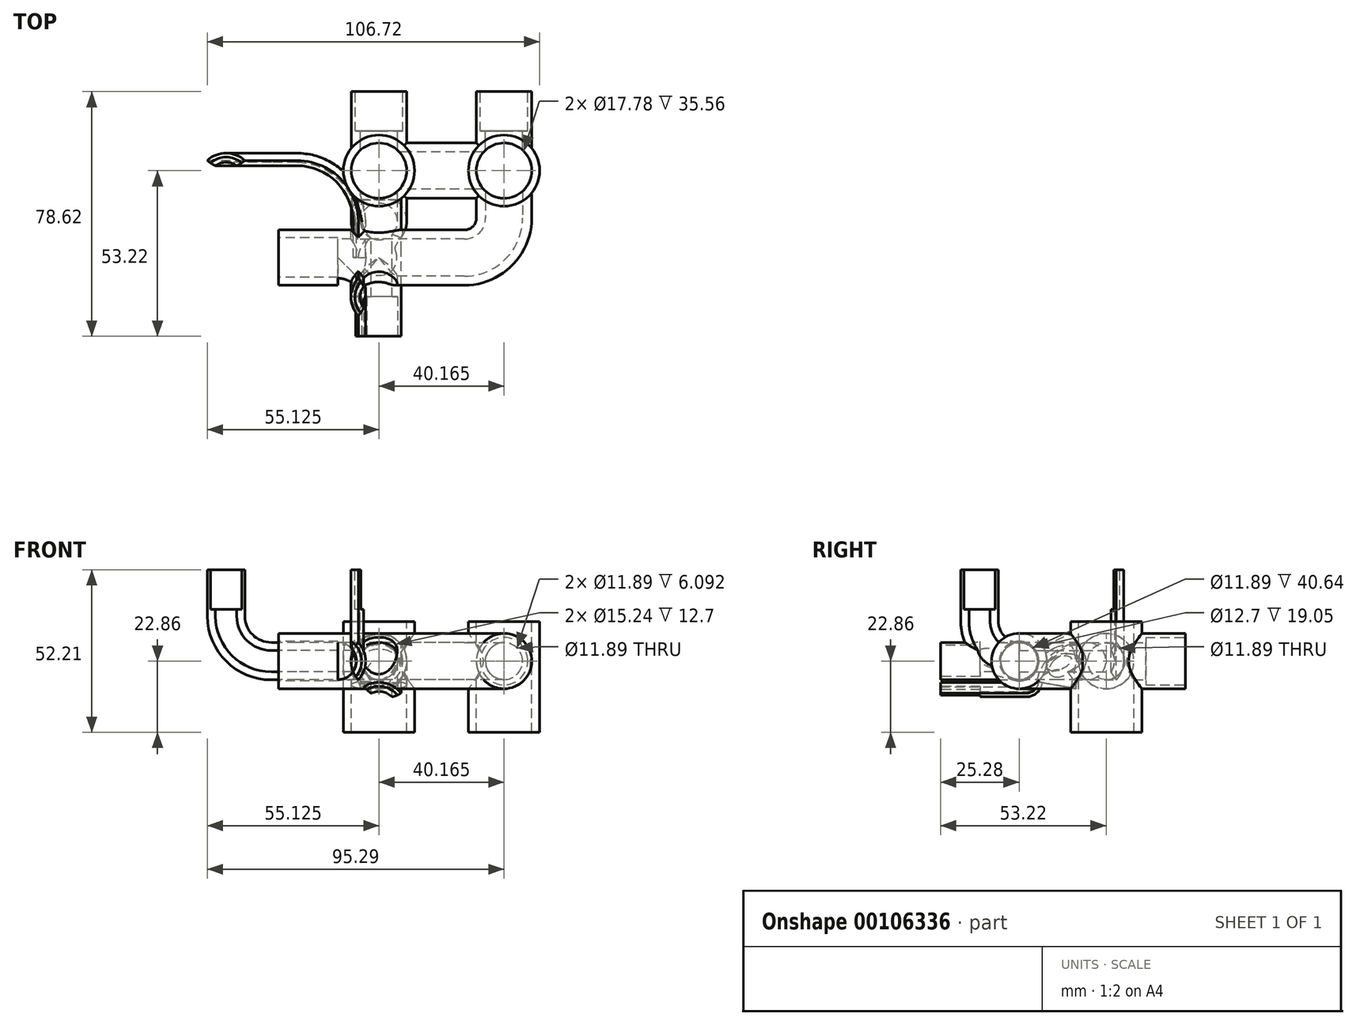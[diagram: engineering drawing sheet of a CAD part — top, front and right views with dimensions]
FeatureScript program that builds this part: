
annotation { "Feature Type Name" : "Feature", "Feature Type Description" : "" }
export const myFeature = defineFeature(function(context is Context, id is Id, definition is map)
    precondition{}
    {
        {
            var Q0;
            Q0=qCreatedBy(makeId("Front.planeOp"),FACE);
            var sketch = newSketch(context, id + "F0", { "sketchPlane" : qUnion([Q0])});
            skCircle(sketch, "E0", {"center": v(0, 0) * mm, "radius": 5.94 * mm});
            skCircle(sketch, "E1", {"center": v(0, 0) * mm, "radius": 8.9 * mm});
            skLineSegment(sketch, "E2", {"start": v(0, 0) * mm, "end": v(17.78, 0) * mm});
            skCircle(sketch, "E3", {"center": v(17.78, 0) * mm, "radius": 8.9 * mm});
            skCircle(sketch, "E4", {"center": v(17.78, 0) * mm, "radius": 5.94 * mm});
            skSolve(sketch);
        }
        {
            var Q0;
            Q0=qCreatedBy(makeId("Top.planeOp"),FACE);
            var sketch = newSketch(context, id + "F1", { "sketchPlane" : qUnion([Q0])});
            skLineSegment(sketch, "E5", {"start": v(0, 0) * mm, "end": v(0, -7.62) * mm});
            skLineSegment(sketch, "E6", {"start": v(17.78, 0) * mm, "end": v(17.78, -7.62) * mm});
            skArc(sketch, "E7", {"start": v(0, -7.62) * mm, "mid": v(-3.72, -16.6) * mm, "end": v(-12.7, -20.32) * mm});
            skLineSegment(sketch, "E8", {"start": v(-12.7, -20.32) * mm, "end": v(-53.34, -20.32) * mm});
            skLineSegment(sketch, "E9", {"start": v(-53.34, -20.32) * mm, "end": v(-53.34, -33.02) * mm});
            skArc(sketch, "E10", {"start": v(-53.34, -33.02) * mm, "mid": v(-50.36, -40.2) * mm, "end": v(-43.18, -43.18) * mm});
            skLineSegment(sketch, "E11", {"start": v(-43.18, -43.18) * mm, "end": v(-29.6, -43.18) * mm});
            skArc(sketch, "E12", {"start": v(0, -43.18) * mm, "mid": v(12.57, -37.97) * mm, "end": v(17.78, -25.4) * mm});
            skLineSegment(sketch, "E13", {"start": v(17.78, -25.4) * mm, "end": v(17.78, -7.62) * mm});
            skLineSegment(sketch, "E14", {"start": v(-43.18, -43.18) * mm, "end": v(-43.18, -20.32) * mm});
            skLineSegment(sketch, "E15", {"start": v(-43.18, -43.18) * mm, "end": v(-74.7, -43.18) * mm});
            skArc(sketch, "E16", {"start": v(-53.34, -20.32) * mm, "mid": v(-57.06, -11.34) * mm, "end": v(-66.04, -7.62) * mm});
            skLineSegment(sketch, "E17", {"start": v(17.78, -25.4) * mm, "end": v(17.78, -62.46) * mm});
            skArc(sketch, "E18", {"start": v(-21.28, -43.18) * mm, "mid": v(-12.34, -46.92) * mm, "end": v(-8.65, -55.88) * mm});
            skLineSegment(sketch, "E19", {"start": v(-8.65, -55.88) * mm, "end": v(-8.65, -62.46) * mm});
            skLineSegment(sketch, "E20", {"start": v(-8.65, -62.46) * mm, "end": v(17.78, -62.46) * mm});
            skLineSegment(sketch, "E21", {"start": v(-29.6, -43.18) * mm, "end": v(-21.28, -43.18) * mm});
            skLineSegment(sketch, "E22", {"start": v(-53.34, -20.32) * mm, "end": v(-53.34, -8.9) * mm});
            skArc(sketch, "E23", {"start": v(-53.34, -8.9) * mm, "mid": v(-57.21, 0.46) * mm, "end": v(-66.57, 4.34) * mm});
            skArc(sketch, "E24", {"start": v(-66.57, 4.34) * mm, "mid": v(-77.3, 9.13) * mm, "end": v(-80.9, 20.32) * mm});
            skLineSegment(sketch, "E25", {"start": v(-80.9, 20.32) * mm, "end": v(-80.9, 25.31) * mm});
            skLineSegment(sketch, "E26", {"start": v(-66.57, 4.34) * mm, "end": v(-72.83, 4.34) * mm});
            skSolve(sketch);
        }
        {
            var Q0;
            Q0=qCreatedBy(makeId("Front.planeOp"),FACE);
            cPlane(context, id + "F2", {"entities" : qUnion([Q0]), "cplaneType" : CPlaneType.OFFSET, "offset" : 20.32 * mm, "width" : 152.4 * mm, "height" : 152.4 * mm});
        }
        {
            var Q0;
            Q0=qCreatedBy(id+"F2.planeOp",FACE);
            var sketch = newSketch(context, id + "F3", { "sketchPlane" : qUnion([Q0])});
            skCircle(sketch, "E27", {"center": v(-53.34, 0) * mm, "radius": 8.9 * mm});
            skCircle(sketch, "E28", {"center": v(-53.34, 0) * mm, "radius": 5.94 * mm});
            skLineSegment(sketch, "E29", {"start": v(-47.4, 0) * mm, "end": v(-46.2, 0) * mm});
            skLineSegment(sketch, "E30", {"start": v(-46.2, 0) * mm, "end": v(-40.26, 0) * mm});
            skCircle(sketch, "E31", {"center": v(-40.26, 0) * mm, "radius": 5.94 * mm});
            skCircle(sketch, "E32", {"center": v(-40.26, 0) * mm, "radius": 8.9 * mm});
            skSolve(sketch);
        }
        {
            var Q0;
            Q0=qCreatedBy(makeId("Right.planeOp"),FACE);
            cPlane(context, id + "F4", {"entities" : qUnion([Q0]), "cplaneType" : CPlaneType.OFFSET, "offset" : 40.13 * mm, "oppositeDirection" : true, "width" : 152.4 * mm, "height" : 152.4 * mm});
        }
        {
            var Q0;
            Q0=qCreatedBy(id+"F4.planeOp",FACE);
            var sketch = newSketch(context, id + "F5", { "sketchPlane" : qUnion([Q0])});
            skLineSegment(sketch, "E33", {"start": v(-20.32, 0) * mm, "end": v(-20.35, 0) * mm});
            skArc(sketch, "E34", {"start": v(-20.35, 0) * mm, "mid": v(-29.33, 3.72) * mm, "end": v(-33.05, 12.7) * mm});
            skLineSegment(sketch, "E35", {"start": v(-33.05, 12.7) * mm, "end": v(-33.05, 16.67) * mm});
            skLineSegment(sketch, "E36", {"start": v(-20.32, 0) * mm, "end": v(-20.32, 16.9) * mm});
            skArc(sketch, "E37", {"start": v(-33.05, 16.67) * mm, "mid": v(-36.77, 25.65) * mm, "end": v(-45.75, 29.37) * mm});
            skLineSegment(sketch, "E38", {"start": v(-45.75, 29.37) * mm, "end": v(-51.61, 29.37) * mm});
            skLineSegment(sketch, "E39", {"start": v(-20.32, 0) * mm, "end": v(-35.47, 0) * mm});
            skLineSegment(sketch, "E40", {"start": v(-51.61, 29.37) * mm, "end": v(-51.61, 0) * mm});
            skSolve(sketch);
        }
        {
            var Q0;
            Q0=sQuery(id+"F1.wireOp",EDGE,"E9");
            cPlane(context, id + "F6", {"entities" : qUnion([Q0]), "cplaneType" : CPlaneType.LINE_ANGLE, "offset" : 25.4 * mm, "angle" : 315 * degree, "width" : 152.4 * mm, "height" : 152.4 * mm});
        }
        {
            var Q0;
            Q0=qCreatedBy(id+"F6.planeOp",FACE);
            var sketch = newSketch(context, id + "F7", { "sketchPlane" : qUnion([Q0])});
            skLineSegment(sketch, "E41", {"start": v(20.32, 37.72) * mm, "end": v(13.72, 37.72) * mm});
            skArc(sketch, "E42", {"start": v(13.72, 37.72) * mm, "mid": v(-7.04, 58.48) * mm, "end": v(13.72, 79.24) * mm});
            skLineSegment(sketch, "E43", {"start": v(13.72, 79.24) * mm, "end": v(51.6, 79.24) * mm});
            skSolve(sketch);
        }
        {
            var Q0;
            Q0=sQuery(id+"F7.wireOp",EDGE,"E43");
            cPlane(context, id + "F8", {"entities" : qUnion([Q0]), "cplaneType" : CPlaneType.LINE_ANGLE, "offset" : 25.4 * mm, "angle" : 90 * degree, "width" : 152.4 * mm, "height" : 152.4 * mm});
        }
        {
            var Q0;
            Q0=sQuery(id+"F7.wireOp",EDGE,"E43");
            cPlane(context, id + "F9", {"entities" : qUnion([Q0]), "cplaneType" : CPlaneType.LINE_ANGLE, "offset" : 25.4 * mm, "angle" : 0 * degree, "width" : 152.4 * mm, "height" : 152.4 * mm});
        }
        {
            var Q0;
            Q0=sQuery(id+"F1.wireOp",EDGE,"E9");
            cPlane(context, id + "F10", {"entities" : qUnion([Q0]), "cplaneType" : CPlaneType.LINE_ANGLE, "offset" : 25.4 * mm, "angle" : 310 * degree, "width" : 152.4 * mm, "height" : 152.4 * mm});
        }
        {
            var Q0;
            Q0=qCreatedBy(id+"F10.planeOp",FACE);
            var sketch = newSketch(context, id + "F11", { "sketchPlane" : qUnion([Q0])});
            skLineSegment(sketch, "E44", {"start": v(20.32, 34.29) * mm, "end": v(45.72, 34.29) * mm});
            skArc(sketch, "E45", {"start": v(45.72, 34.29) * mm, "mid": v(55.97, 24.04) * mm, "end": v(45.72, 13.79) * mm});
            skLineSegment(sketch, "E46", {"start": v(45.72, 13.79) * mm, "end": v(0, 13.79) * mm});
            skSolve(sketch);
        }
        {
            var Q0;
            Q0=sQuery(id+"F11.wireOp",EDGE,"E46");
            cPlane(context, id + "F12", {"entities" : qUnion([Q0]), "cplaneType" : CPlaneType.LINE_ANGLE, "offset" : 25.4 * mm, "angle" : 90 * degree, "width" : 152.4 * mm, "height" : 152.4 * mm});
        }
        {
            var Q0;
            Q0=qCreatedBy(id+"F12.planeOp",FACE);
            var sketch = newSketch(context, id + "F13", { "sketchPlane" : qUnion([Q0])});
            skLineSegment(sketch, "E47", {"start": v(-45.72, -15.7) * mm, "end": v(-18.13, -15.7) * mm});
            skArc(sketch, "E48", {"start": v(-18.13, -15.7) * mm, "mid": v(-11.95, -13.42) * mm, "end": v(-8.73, -7.66) * mm});
            skArc(sketch, "E49", {"start": v(-8.73, -7.66) * mm, "mid": v(-5.75, -2.25) * mm, "end": v(0, 0) * mm});
            skLineSegment(sketch, "E50", {"start": v(0, 0) * mm, "end": v(0, 3.02) * mm});
            skLineSegment(sketch, "E51", {"start": v(-18.13, -15.7) * mm, "end": v(0, -15.7) * mm});
            skLineSegment(sketch, "E52", {"start": v(0, 0) * mm, "end": v(0, -15.7) * mm});
            skSolve(sketch);
        }
        {
            var Q0;
            Q0=sQuery(id+"F13.wireOp",EDGE,"E50");
            cPlane(context, id + "F14", {"entities" : qUnion([Q0]), "cplaneType" : CPlaneType.LINE_ANGLE, "offset" : 25.4 * mm, "angle" : 90 * degree, "width" : 152.4 * mm, "height" : 152.4 * mm});
        }
        {
            var Q0;
            Q0=qCreatedBy(id+"F14.planeOp",FACE);
            var sketch = newSketch(context, id + "F15", { "sketchPlane" : qUnion([Q0])});
            skCircle(sketch, "E53", {"center": v(40.17, 0) * mm, "radius": 8.9 * mm});
            skCircle(sketch, "E54", {"center": v(40.17, 0) * mm, "radius": 5.94 * mm});
            skSolve(sketch);
        }
        {
            var Q0;
            {var subQ0=sQuery(id+"F3.wireOp",EDGE,"E32");var subQ1=sQuery(id+"F3.wireOp",EDGE,"E27");var subQ2=makeQuery(id+"F3.imprint","INTERSECT",VERTEX,{"disambiguationData":[OD(0.0)],"derivedFrom":[subQ1,subQ0]});Q0=makeQuery(id+"F3.imprint","IMPRINT",FACE,{"disambiguationData":[TD([[makeQuery(id+"F3.imprint","IMPRINT",EDGE,{"disambiguationData":[TD([[subQ2,-1.0]])],"derivedFrom":subQ1}),1.0]])]});}
            var Q1;
            {var subQ1=sQuery(id+"F3.wireOp",EDGE,"E29");Q1=makeQuery(id+"F3.imprint","IMPRINT",FACE,{"disambiguationData":[TD([[makeQuery(id+"F3.imprint","IMPRINT",EDGE,{"derivedFrom":subQ1}),1.0]])]});}
            var Q2;
            {var subQ0=sQuery(id+"F3.wireOp",EDGE,"E30");var subQ1=sQuery(id+"F3.wireOp",EDGE,"E27");var subQ2=makeQuery(id+"F3.imprint","INTERSECT",VERTEX,{"derivedFrom":[subQ1,subQ0]});Q2=makeQuery(id+"F3.imprint","IMPRINT",FACE,{"disambiguationData":[TD([[makeQuery(id+"F3.imprint","IMPRINT",EDGE,{"disambiguationData":[TD([[subQ2,-1.0]])],"derivedFrom":subQ1}),1.0]])]});}
            var Q3;
            {var subQ0=sQuery(id+"F3.wireOp",EDGE,"E30");var subQ1=sQuery(id+"F3.wireOp",EDGE,"E27");var subQ2=makeQuery(id+"F3.imprint","INTERSECT",VERTEX,{"derivedFrom":[subQ1,subQ0]});Q3=makeQuery(id+"F3.imprint","IMPRINT",FACE,{"disambiguationData":[TD([[makeQuery(id+"F3.imprint","IMPRINT",EDGE,{"disambiguationData":[TD([[subQ2,1.0]])],"derivedFrom":subQ1}),1.0]])]});}
            var Q4;
            {var subQ1=sQuery(id+"F3.wireOp",EDGE,"E29");Q4=makeQuery(id+"F3.imprint","IMPRINT",FACE,{"disambiguationData":[TD([[makeQuery(id+"F3.imprint","IMPRINT",EDGE,{"derivedFrom":subQ1}),-1.0]])]});}
            var Q5;
            Q5=sQuery(id+"F11.wireOp",EDGE,"E44");
            var Q6;
            Q6=sQuery(id+"F11.wireOp",EDGE,"E45");
            var Q7;
            Q7=sQuery(id+"F13.wireOp",EDGE,"E47");
            var Q8;
            Q8=sQuery(id+"F13.wireOp",EDGE,"E48");
            var Q9;
            Q9=sQuery(id+"F13.wireOp",EDGE,"E49");
            sweep(context, id + "F16", {"profiles" : qUnion([Q0, Q1, Q2, Q3, Q4]), "path" : qUnion([Q5, Q6, Q7, Q8, Q9])});
        }
        {
            var Q0;
            Q0=makeQuery(id+"F15.imprint","IMPRINT",FACE,{"disambiguationData":[TD([[makeQuery(id+"F15.imprint","IMPRINT",EDGE,{"derivedFrom":sQuery(id+"F15.wireOp",EDGE,"E53")}),1.0]])]});
            var Q1;
            Q1=sQuery(id+"F13.wireOp",EDGE,"E49");
            sweep(context, id + "F17", {"operationType" : NewBodyOperationType.ADD, "profiles" : qUnion([Q0]), "path" : qUnion([Q1])});
        }
        {
            var Q0;
            {var subQ0=sQuery(id+"F3.wireOp",EDGE,"E32");var subQ1=sQuery(id+"F3.wireOp",EDGE,"E27");var subQ2=makeQuery(id+"F3.imprint","INTERSECT",VERTEX,{"disambiguationData":[OD(0.0)],"derivedFrom":[subQ1,subQ0]});Q0=makeQuery(id+"F3.imprint","IMPRINT",FACE,{"disambiguationData":[TD([[makeQuery(id+"F3.imprint","IMPRINT",EDGE,{"disambiguationData":[TD([[subQ2,1.0]])],"derivedFrom":subQ1}),-1.0]])]});}
            var Q1;
            {var subQ1=sQuery(id+"F3.wireOp",EDGE,"E29");Q1=makeQuery(id+"F3.imprint","IMPRINT",FACE,{"disambiguationData":[TD([[makeQuery(id+"F3.imprint","IMPRINT",EDGE,{"derivedFrom":subQ1}),1.0]])]});}
            var Q2;
            {var subQ0=sQuery(id+"F3.wireOp",EDGE,"E28");var subQ1=makeQuery(id+"F3.imprint","INTERSECT",VERTEX,{"derivedFrom":[subQ0,sQuery(id+"F3.wireOp",EDGE,"E29")]});Q2=makeQuery(id+"F3.imprint","IMPRINT",FACE,{"disambiguationData":[TD([[makeQuery(id+"F3.imprint","IMPRINT",EDGE,{"disambiguationData":[TD([[subQ1,-1.0]])],"derivedFrom":subQ0}),1.0]])]});}
            var Q3;
            {var subQ1=sQuery(id+"F3.wireOp",EDGE,"E29");Q3=makeQuery(id+"F3.imprint","IMPRINT",FACE,{"disambiguationData":[TD([[makeQuery(id+"F3.imprint","IMPRINT",EDGE,{"derivedFrom":subQ1}),-1.0]])]});}
            var Q4;
            Q4=sQuery(id+"F5.wireOp",EDGE,"E34");
            var Q5;
            Q5=sQuery(id+"F5.wireOp",EDGE,"E35");
            sweep(context, id + "F18", {"operationType" : NewBodyOperationType.ADD, "profiles" : qUnion([Q0, Q1, Q2, Q3]), "path" : qUnion([Q4, Q5])});
        }
        {
            var Q0;
            {var subQ0=sQuery(id+"F3.wireOp",EDGE,"E28");var subQ1=makeQuery(id+"F3.imprint","INTERSECT",VERTEX,{"derivedFrom":[subQ0,sQuery(id+"F3.wireOp",EDGE,"E29")]});Q0=makeQuery(id+"F3.imprint","IMPRINT",FACE,{"disambiguationData":[TD([[makeQuery(id+"F3.imprint","IMPRINT",EDGE,{"disambiguationData":[TD([[subQ1,-1.0]])],"derivedFrom":subQ0}),1.0]])]});}
            var Q1;
            {var subQ1=sQuery(id+"F3.wireOp",EDGE,"E29");Q1=makeQuery(id+"F3.imprint","IMPRINT",FACE,{"disambiguationData":[TD([[makeQuery(id+"F3.imprint","IMPRINT",EDGE,{"derivedFrom":subQ1}),1.0]])]});}
            var Q2;
            {var subQ0=sQuery(id+"F3.wireOp",EDGE,"E32");var subQ1=sQuery(id+"F3.wireOp",EDGE,"E27");var subQ2=makeQuery(id+"F3.imprint","INTERSECT",VERTEX,{"disambiguationData":[OD(0.0)],"derivedFrom":[subQ1,subQ0]});Q2=makeQuery(id+"F3.imprint","IMPRINT",FACE,{"disambiguationData":[TD([[makeQuery(id+"F3.imprint","IMPRINT",EDGE,{"disambiguationData":[TD([[subQ2,1.0]])],"derivedFrom":subQ1}),-1.0]])]});}
            var Q3;
            {var subQ1=sQuery(id+"F3.wireOp",EDGE,"E29");Q3=makeQuery(id+"F3.imprint","IMPRINT",FACE,{"disambiguationData":[TD([[makeQuery(id+"F3.imprint","IMPRINT",EDGE,{"derivedFrom":subQ1}),-1.0]])]});}
            var Q4;
            Q4=sQuery(id+"F5.wireOp",EDGE,"E34");
            var Q5;
            Q5=sQuery(id+"F5.wireOp",EDGE,"E35");
            sweep(context, id + "F19", {"operationType" : NewBodyOperationType.ADD, "profiles" : qUnion([Q0, Q1, Q2, Q3]), "path" : qUnion([Q4, Q5])});
        }
        {
            var Q0;
            Q0=sQuery(id+"F1.wireOp",EDGE,"E9");
            cPlane(context, id + "F20", {"entities" : qUnion([Q0]), "cplaneType" : CPlaneType.LINE_ANGLE, "offset" : 25.4 * mm, "angle" : 90 * degree, "width" : 152.4 * mm, "height" : 152.4 * mm});
        }
        {
            var Q0;
            Q0=qCreatedBy(id+"F20.planeOp",FACE);
            var sketch = newSketch(context, id + "F21", { "sketchPlane" : qUnion([Q0])});
            skCircle(sketch, "E55", {"center": v(-20.32, 0) * mm, "radius": 6.35 * mm});
            skCircle(sketch, "E56", {"center": v(-20.32, 0) * mm, "radius": 8.9 * mm});
            skSolve(sketch);
        }
        {
            var Q0;
            Q0=qCreatedBy(makeId("Top.planeOp"),FACE);
            var sketch = newSketch(context, id + "F22", { "sketchPlane" : qUnion([Q0])});
            skLineSegment(sketch, "E57", {"start": v(-53.34, -20.32) * mm, "end": v(-72.4, -20.32) * mm});
            skSolve(sketch);
        }
        {
            var Q0;
            Q0=makeQuery(id+"F0.imprint","IMPRINT",FACE,{"disambiguationData":[TD([[makeQuery(id+"F0.imprint","IMPRINT",EDGE,{"derivedFrom":sQuery(id+"F0.wireOp",EDGE,"E0")}),1.0]])]});
            var Q1;
            Q1=sQuery(id+"F1.wireOp",EDGE,"E5");
            var Q2;
            Q2=sQuery(id+"F1.wireOp",EDGE,"E7");
            var Q3;
            Q3=sQuery(id+"F1.wireOp",EDGE,"E8");
            sweep(context, id + "F23", {"operationType" : NewBodyOperationType.REMOVE, "profiles" : qUnion([Q0]), "path" : qUnion([Q1, Q2, Q3])});
        }
        {
            var Q0;
            Q0=makeQuery(id+"F0.imprint","IMPRINT",FACE,{"disambiguationData":[TD([[makeQuery(id+"F0.imprint","IMPRINT",EDGE,{"derivedFrom":sQuery(id+"F0.wireOp",EDGE,"E0")}),-1.0]])]});
            var Q1;
            Q1=sQuery(id+"F1.wireOp",EDGE,"E5");
            var Q2;
            Q2=sQuery(id+"F1.wireOp",EDGE,"E7");
            var Q3;
            Q3=sQuery(id+"F1.wireOp",EDGE,"E8");
            sweep(context, id + "F24", {"operationType" : NewBodyOperationType.ADD, "profiles" : qUnion([Q0]), "path" : qUnion([Q1, Q2, Q3])});
        }
        {
            var Q0;
            Q0=makeQuery(id+"F15.imprint","IMPRINT",FACE,{"disambiguationData":[TD([[makeQuery(id+"F15.imprint","IMPRINT",EDGE,{"derivedFrom":sQuery(id+"F15.wireOp",EDGE,"E54")}),1.0]])]});
            var Q1;
            Q1=sQuery(id+"F11.wireOp",EDGE,"E44");
            var Q2;
            Q2=sQuery(id+"F11.wireOp",EDGE,"E45");
            var Q3;
            Q3=sQuery(id+"F13.wireOp",EDGE,"E49");
            var Q4;
            Q4=sQuery(id+"F13.wireOp",EDGE,"E48");
            var Q5;
            Q5=sQuery(id+"F13.wireOp",EDGE,"E47");
            sweep(context, id + "F25", {"operationType" : NewBodyOperationType.REMOVE, "profiles" : qUnion([Q0]), "path" : qUnion([Q1, Q2, Q3, Q4, Q5])});
        }
        {
            var Q0;
            {var subQ0=sQuery(id+"F3.wireOp",EDGE,"E27");var subQ1=makeQuery(id+"F3.imprint","INTERSECT",VERTEX,{"derivedFrom":[subQ0,sQuery(id+"F3.wireOp",EDGE,"E30")]});Q0=makeQuery(id+"F3.imprint","IMPRINT",FACE,{"disambiguationData":[TD([[makeQuery(id+"F3.imprint","IMPRINT",EDGE,{"disambiguationData":[TD([[subQ1,-1.0]])],"derivedFrom":subQ0}),-1.0]])]});}
            var Q1;
            {var subQ0=sQuery(id+"F3.wireOp",EDGE,"E30");var subQ1=sQuery(id+"F3.wireOp",EDGE,"E27");var subQ2=makeQuery(id+"F3.imprint","INTERSECT",VERTEX,{"derivedFrom":[subQ1,subQ0]});Q1=makeQuery(id+"F3.imprint","IMPRINT",FACE,{"disambiguationData":[TD([[makeQuery(id+"F3.imprint","IMPRINT",EDGE,{"disambiguationData":[TD([[subQ2,-1.0]])],"derivedFrom":subQ1}),1.0]])]});}
            var Q2;
            {var subQ0=sQuery(id+"F3.wireOp",EDGE,"E30");var subQ1=sQuery(id+"F3.wireOp",EDGE,"E27");var subQ2=makeQuery(id+"F3.imprint","INTERSECT",VERTEX,{"derivedFrom":[subQ1,subQ0]});Q2=makeQuery(id+"F3.imprint","IMPRINT",FACE,{"disambiguationData":[TD([[makeQuery(id+"F3.imprint","IMPRINT",EDGE,{"disambiguationData":[TD([[subQ2,1.0]])],"derivedFrom":subQ1}),1.0]])]});}
            var Q3;
            Q3=sQuery(id+"F5.wireOp",EDGE,"E34");
            var Q4;
            Q4=sQuery(id+"F5.wireOp",EDGE,"E35");
            var Q5;
            Q5=sQuery(id+"F5.wireOp",EDGE,"E37");
            sweep(context, id + "F26", {"operationType" : NewBodyOperationType.REMOVE, "profiles" : qUnion([Q0, Q1, Q2]), "path" : qUnion([Q3, Q4, Q5])});
        }
        {
            var Q0;
            Q0=makeQuery(id+"F21.imprint","IMPRINT",FACE,{"disambiguationData":[TD([[makeQuery(id+"F21.imprint","IMPRINT",EDGE,{"derivedFrom":sQuery(id+"F21.wireOp",EDGE,"E55")}),1.0]])]});
            var Q1;
            Q1=sQuery(id+"F22.wireOp",EDGE,"E57");
            sweep(context, id + "F27", {"operationType" : NewBodyOperationType.REMOVE, "profiles" : qUnion([Q0]), "path" : qUnion([Q1])});
        }
        {
            var Q0;
            {var subQ0=sQuery(id+"F3.wireOp",EDGE,"E32");var subQ1=sQuery(id+"F3.wireOp",EDGE,"E28");var subQ2=makeQuery(id+"F3.imprint","INTERSECT",VERTEX,{"disambiguationData":[OD(0.0)],"derivedFrom":[subQ1,subQ0]});Q0=makeQuery(id+"F3.imprint","IMPRINT",FACE,{"disambiguationData":[TD([[makeQuery(id+"F3.imprint","IMPRINT",EDGE,{"disambiguationData":[TD([[subQ2,-1.0]])],"derivedFrom":subQ1}),1.0]])]});}
            var Q1;
            {var subQ0=sQuery(id+"F3.wireOp",EDGE,"E28");var subQ1=makeQuery(id+"F3.imprint","INTERSECT",VERTEX,{"derivedFrom":[subQ0,sQuery(id+"F3.wireOp",EDGE,"E29")]});Q1=makeQuery(id+"F3.imprint","IMPRINT",FACE,{"disambiguationData":[TD([[makeQuery(id+"F3.imprint","IMPRINT",EDGE,{"disambiguationData":[TD([[subQ1,-1.0]])],"derivedFrom":subQ0}),1.0]])]});}
            var Q2;
            Q2=sQuery(id+"F7.wireOp",EDGE,"E41");
            var Q3;
            Q3=sQuery(id+"F7.wireOp",EDGE,"E42");
            sweep(context, id + "F28", {"operationType" : NewBodyOperationType.REMOVE, "profiles" : qUnion([Q0, Q1]), "path" : qUnion([Q2, Q3])});
        }
        {
            var Q0;
            Q0=makeQuery(id+"F21.imprint","IMPRINT",FACE,{"disambiguationData":[TD([[makeQuery(id+"F21.imprint","IMPRINT",EDGE,{"derivedFrom":sQuery(id+"F21.wireOp",EDGE,"E55")}),-1.0]])]});
            var Q1;
            Q1=sQuery(id+"F22.wireOp",EDGE,"E57");
            sweep(context, id + "F29", {"operationType" : NewBodyOperationType.ADD, "profiles" : qUnion([Q0]), "path" : qUnion([Q1])});
        }
        {
            var Q0;
            {var subQ0=sQuery(id+"F3.wireOp",EDGE,"E32");var subQ1=sQuery(id+"F3.wireOp",EDGE,"E28");var subQ2=makeQuery(id+"F3.imprint","INTERSECT",VERTEX,{"disambiguationData":[OD(0.0)],"derivedFrom":[subQ1,subQ0]});Q0=makeQuery(id+"F3.imprint","IMPRINT",FACE,{"disambiguationData":[TD([[makeQuery(id+"F3.imprint","IMPRINT",EDGE,{"disambiguationData":[TD([[subQ2,-1.0]])],"derivedFrom":subQ1}),1.0]])]});}
            var Q1;
            {var subQ0=sQuery(id+"F3.wireOp",EDGE,"E28");var subQ1=makeQuery(id+"F3.imprint","INTERSECT",VERTEX,{"derivedFrom":[subQ0,sQuery(id+"F3.wireOp",EDGE,"E29")]});Q1=makeQuery(id+"F3.imprint","IMPRINT",FACE,{"disambiguationData":[TD([[makeQuery(id+"F3.imprint","IMPRINT",EDGE,{"disambiguationData":[TD([[subQ1,-1.0]])],"derivedFrom":subQ0}),1.0]])]});}
            var Q2;
            Q2=sQuery(id+"F7.wireOp",EDGE,"E42");
            var Q3;
            Q3=sQuery(id+"F7.wireOp",EDGE,"E41");
            sweep(context, id + "F30", {"operationType" : NewBodyOperationType.REMOVE, "profiles" : qUnion([Q0, Q1]), "path" : qUnion([Q2, Q3])});
        }
        {
            var Q0;
            {var subQ0=sQuery(id+"F3.wireOp",EDGE,"E32");var subQ1=sQuery(id+"F3.wireOp",EDGE,"E28");var subQ2=makeQuery(id+"F3.imprint","INTERSECT",VERTEX,{"disambiguationData":[OD(0.0)],"derivedFrom":[subQ1,subQ0]});Q0=makeQuery(id+"F3.imprint","IMPRINT",FACE,{"disambiguationData":[TD([[makeQuery(id+"F3.imprint","IMPRINT",EDGE,{"disambiguationData":[TD([[subQ2,-1.0]])],"derivedFrom":subQ1}),1.0]])]});}
            var Q1;
            {var subQ0=sQuery(id+"F3.wireOp",EDGE,"E28");var subQ1=makeQuery(id+"F3.imprint","INTERSECT",VERTEX,{"derivedFrom":[subQ0,sQuery(id+"F3.wireOp",EDGE,"E29")]});Q1=makeQuery(id+"F3.imprint","IMPRINT",FACE,{"disambiguationData":[TD([[makeQuery(id+"F3.imprint","IMPRINT",EDGE,{"disambiguationData":[TD([[subQ1,-1.0]])],"derivedFrom":subQ0}),1.0]])]});}
            var Q2;
            Q2=sQuery(id+"F11.wireOp",EDGE,"E45");
            var Q3;
            Q3=sQuery(id+"F11.wireOp",EDGE,"E44");
            sweep(context, id + "F31", {"operationType" : NewBodyOperationType.REMOVE, "profiles" : qUnion([Q0, Q1]), "path" : qUnion([Q2, Q3])});
        }
        {
            var Q0;
            Q0=qCreatedBy(makeId("Top.planeOp"),FACE);
            var sketch = newSketch(context, id + "F32", { "sketchPlane" : qUnion([Q0])});
            skLineSegment(sketch, "E58", {"start": v(0, 0) * mm, "end": v(0, 7.62) * mm});
            skLineSegment(sketch, "E59", {"start": v(-40.17, 0) * mm, "end": v(-40.17, 7.62) * mm});
            skCircle(sketch, "E60", {"center": v(-40.17, 7.62) * mm, "radius": 8.9 * mm});
            skCircle(sketch, "E61", {"center": v(0, 7.62) * mm, "radius": 8.9 * mm});
            skCircle(sketch, "E62", {"center": v(0, 7.62) * mm, "radius": 11.43 * mm});
            skCircle(sketch, "E63", {"center": v(-40.17, 7.62) * mm, "radius": 11.43 * mm});
            skSolve(sketch);
        }
        {
            var Q0;
            Q0=sQuery(id+"F32.wireOp",EDGE,"E59");
            cPlane(context, id + "F33", {"entities" : qUnion([Q0]), "cplaneType" : CPlaneType.LINE_ANGLE, "offset" : 25.4 * mm, "angle" : 90 * degree, "width" : 152.4 * mm, "height" : 152.4 * mm});
        }
        {
            var Q0;
            Q0=qCreatedBy(id+"F33.planeOp",FACE);
            var sketch = newSketch(context, id + "F34", { "sketchPlane" : qUnion([Q0])});
            skLineSegment(sketch, "E64", {"start": v(7.62, 0) * mm, "end": v(7.62, 4.48) * mm});
            skSolve(sketch);
        }
        {
            var Q0;
            Q0=sQuery(id+"F34.wireOp",EDGE,"E64");
            cPlane(context, id + "F35", {"entities" : qUnion([Q0]), "cplaneType" : CPlaneType.LINE_ANGLE, "offset" : 25.4 * mm, "angle" : 135 * degree, "width" : 152.4 * mm, "height" : 152.4 * mm});
        }
        {
            var Q0;
            Q0=makeQuery(id+"F32.imprint","IMPRINT",FACE,{"disambiguationData":[TD([[makeQuery(id+"F32.imprint","IMPRINT",EDGE,{"derivedFrom":sQuery(id+"F32.wireOp",EDGE,"E60")}),-1.0]])]});
            extrude(context, id + "F36", {"entities" : qUnion([Q0]), "operationType" : NewBodyOperationType.ADD, "oppositeDirection" : true, "depth" : 22.86 * mm});
        }
        {
            var Q0;
            Q0=makeQuery(id+"F32.imprint","IMPRINT",FACE,{"disambiguationData":[TD([[makeQuery(id+"F32.imprint","IMPRINT",EDGE,{"derivedFrom":sQuery(id+"F32.wireOp",EDGE,"E61")}),-1.0]])]});
            extrude(context, id + "F37", {"entities" : qUnion([Q0]), "operationType" : NewBodyOperationType.ADD, "oppositeDirection" : true, "depth" : 22.86 * mm});
        }
        {
            var Q0;
            Q0=qCreatedBy(makeId("Front.planeOp"),FACE);
            cPlane(context, id + "F38", {"entities" : qUnion([Q0]), "cplaneType" : CPlaneType.OFFSET, "offset" : 7.62 * mm, "oppositeDirection" : true, "width" : 152.4 * mm, "height" : 152.4 * mm});
        }
        {
            var Q0;
            Q0=makeQuery(id+"F32.imprint","IMPRINT",FACE,{"disambiguationData":[TD([[makeQuery(id+"F32.imprint","IMPRINT",EDGE,{"derivedFrom":sQuery(id+"F32.wireOp",EDGE,"E61")}),-1.0]])]});
            extrude(context, id + "F39", {"entities" : qUnion([Q0]), "operationType" : NewBodyOperationType.ADD, "depth" : 12.7 * mm});
        }
        {
            var Q0;
            Q0=makeQuery(id+"F32.imprint","IMPRINT",FACE,{"disambiguationData":[TD([[makeQuery(id+"F32.imprint","IMPRINT",EDGE,{"derivedFrom":sQuery(id+"F32.wireOp",EDGE,"E60")}),-1.0]])]});
            extrude(context, id + "F40", {"entities" : qUnion([Q0]), "operationType" : NewBodyOperationType.ADD, "depth" : 12.7 * mm});
        }
        {
            var Q0;
            Q0=qCreatedBy(makeId("Right.planeOp"),FACE);
            var sketch = newSketch(context, id + "F41", { "sketchPlane" : qUnion([Q0])});
            skCircle(sketch, "E65", {"center": v(7.62, 0) * mm, "radius": 5.94 * mm});
            skCircle(sketch, "E66", {"center": v(7.62, 0) * mm, "radius": 8.9 * mm});
            skSolve(sketch);
        }
        {
            var Q0;
            Q0=qCreatedBy(makeId("Top.planeOp"),FACE);
            var sketch = newSketch(context, id + "F42", { "sketchPlane" : qUnion([Q0])});
            skLineSegment(sketch, "E67", {"start": v(0, 7.62) * mm, "end": v(-40.17, 7.62) * mm});
            skSolve(sketch);
        }
        {
            var Q0;
            Q0=qCreatedBy(id+"F38.planeOp",FACE);
            var sketch = newSketch(context, id + "F43", { "sketchPlane" : qUnion([Q0])});
            skCircle(sketch, "E68", {"center": v(-40.17, 0) * mm, "radius": 5.94 * mm});
            skCircle(sketch, "E69", {"center": v(-40.17, 0) * mm, "radius": 8.9 * mm});
            skCircle(sketch, "E70", {"center": v(0, 0) * mm, "radius": 5.94 * mm});
            skCircle(sketch, "E71", {"center": v(0, 0) * mm, "radius": 8.9 * mm});
            skSolve(sketch);
        }
        {
            var Q0;
            Q0=qCreatedBy(makeId("Top.planeOp"),FACE);
            var sketch = newSketch(context, id + "F44", { "sketchPlane" : qUnion([Q0])});
            skLineSegment(sketch, "E72", {"start": v(0, 7.62) * mm, "end": v(0, 33.02) * mm});
            skLineSegment(sketch, "E73", {"start": v(-40.17, 7.62) * mm, "end": v(-40.17, 33.02) * mm});
            skSolve(sketch);
        }
        {
            var Q0;
            Q0=makeQuery(id+"F43.imprint","IMPRINT",FACE,{"disambiguationData":[TD([[makeQuery(id+"F43.imprint","IMPRINT",EDGE,{"derivedFrom":sQuery(id+"F43.wireOp",EDGE,"E70")}),-1.0]])]});
            var Q1;
            Q1=sQuery(id+"F44.wireOp",EDGE,"E72");
            sweep(context, id + "F45", {"operationType" : NewBodyOperationType.ADD, "profiles" : qUnion([Q0]), "path" : qUnion([Q1])});
        }
        {
            var Q0;
            Q0=makeQuery(id+"F43.imprint","IMPRINT",FACE,{"disambiguationData":[TD([[makeQuery(id+"F43.imprint","IMPRINT",EDGE,{"derivedFrom":sQuery(id+"F43.wireOp",EDGE,"E68")}),-1.0]])]});
            var Q1;
            Q1=sQuery(id+"F44.wireOp",EDGE,"E73");
            sweep(context, id + "F46", {"operationType" : NewBodyOperationType.ADD, "profiles" : qUnion([Q0]), "path" : qUnion([Q1])});
        }
        {
            var Q0;
            Q0=makeQuery(id+"F41.imprint","IMPRINT",FACE,{"disambiguationData":[TD([[makeQuery(id+"F41.imprint","IMPRINT",EDGE,{"derivedFrom":sQuery(id+"F41.wireOp",EDGE,"E65")}),-1.0]])]});
            var Q1;
            Q1=sQuery(id+"F42.wireOp",EDGE,"E67");
            sweep(context, id + "F47", {"operationType" : NewBodyOperationType.ADD, "profiles" : qUnion([Q0]), "path" : qUnion([Q1])});
        }
        {
            var Q0;
            Q0=makeQuery(id+"F32.imprint","IMPRINT",FACE,{"disambiguationData":[TD([[makeQuery(id+"F32.imprint","IMPRINT",EDGE,{"derivedFrom":sQuery(id+"F32.wireOp",EDGE,"E61")}),1.0]])]});
            extrude(context, id + "F48", {"entities" : qUnion([Q0]), "operationType" : NewBodyOperationType.REMOVE, "oppositeDirection" : true, "depth" : 25.4 * mm});
        }
        {
            var Q0;
            Q0=makeQuery(id+"F32.imprint","IMPRINT",FACE,{"disambiguationData":[TD([[makeQuery(id+"F32.imprint","IMPRINT",EDGE,{"derivedFrom":sQuery(id+"F32.wireOp",EDGE,"E61")}),1.0]])]});
            extrude(context, id + "F49", {"entities" : qUnion([Q0]), "operationType" : NewBodyOperationType.REMOVE, "depth" : 25.4 * mm});
        }
        {
            var Q0;
            Q0=makeQuery(id+"F32.imprint","IMPRINT",FACE,{"disambiguationData":[TD([[makeQuery(id+"F32.imprint","IMPRINT",EDGE,{"derivedFrom":sQuery(id+"F32.wireOp",EDGE,"E60")}),1.0]])]});
            var Q1;
            Q1=sQuery(id+"F32.wireOp",EDGE,"E60");
            extrude(context, id + "F50", {"entities" : qUnion([Q0]), "operationType" : NewBodyOperationType.REMOVE, "surfaceEntities" : qUnion([Q1]), "depth" : 25.4 * mm});
        }
        {
            var Q0;
            Q0=makeQuery(id+"F32.imprint","IMPRINT",FACE,{"disambiguationData":[TD([[makeQuery(id+"F32.imprint","IMPRINT",EDGE,{"derivedFrom":sQuery(id+"F32.wireOp",EDGE,"E60")}),1.0]])]});
            extrude(context, id + "F51", {"entities" : qUnion([Q0]), "operationType" : NewBodyOperationType.REMOVE, "oppositeDirection" : true, "depth" : 25.4 * mm});
        }
        {
            var Q0;
            Q0=makeQuery(id+"F43.imprint","IMPRINT",FACE,{"disambiguationData":[TD([[makeQuery(id+"F43.imprint","IMPRINT",EDGE,{"derivedFrom":sQuery(id+"F43.wireOp",EDGE,"E70")}),1.0]])]});
            extrude(context, id + "F52", {"entities" : qUnion([Q0]), "operationType" : NewBodyOperationType.REMOVE, "oppositeDirection" : true, "depth" : 25.4 * mm});
        }
        {
            var Q0;
            Q0=makeQuery(id+"F43.imprint","IMPRINT",FACE,{"disambiguationData":[TD([[makeQuery(id+"F43.imprint","IMPRINT",EDGE,{"derivedFrom":sQuery(id+"F43.wireOp",EDGE,"E68")}),1.0]])]});
            extrude(context, id + "F53", {"entities" : qUnion([Q0]), "operationType" : NewBodyOperationType.REMOVE, "oppositeDirection" : true, "depth" : 34.24 * mm});
        }
        {
            var Q0;
            Q0=makeQuery(id+"F41.imprint","IMPRINT",FACE,{"disambiguationData":[TD([[makeQuery(id+"F41.imprint","IMPRINT",EDGE,{"derivedFrom":sQuery(id+"F41.wireOp",EDGE,"E65")}),1.0]])]});
            extrude(context, id + "F54", {"entities" : qUnion([Q0]), "operationType" : NewBodyOperationType.REMOVE, "oppositeDirection" : true, "depth" : 35.6 * mm});
        }
        {
            var Q0;
            Q0=makeQuery(id+"F43.imprint","IMPRINT",FACE,{"disambiguationData":[TD([[makeQuery(id+"F43.imprint","IMPRINT",EDGE,{"derivedFrom":sQuery(id+"F43.wireOp",EDGE,"E70")}),1.0]])]});
            extrude(context, id + "F55", {"entities" : qUnion([Q0]), "operationType" : NewBodyOperationType.REMOVE, "depth" : 13.84 * mm});
        }
        {
            var Q0;
            Q0=makeQuery(id+"F15.imprint","IMPRINT",FACE,{"disambiguationData":[TD([[makeQuery(id+"F15.imprint","IMPRINT",EDGE,{"derivedFrom":sQuery(id+"F15.wireOp",EDGE,"E54")}),1.0]])]});
            var Q1;
            Q1=sQuery(id+"F15.wireOp",EDGE,"E54");
            var Q2;
            Q2=sQuery(id+"F13.wireOp",EDGE,"E49");
            sweep(context, id + "F56", {"operationType" : NewBodyOperationType.REMOVE, "profiles" : qUnion([Q0]), "surfaceProfiles" : qUnion([Q1]), "path" : qUnion([Q2])});
        }
        {
            var Q0;
            Q0=makeQuery(id+"F43.imprint","IMPRINT",FACE,{"disambiguationData":[TD([[makeQuery(id+"F43.imprint","IMPRINT",EDGE,{"derivedFrom":sQuery(id+"F43.wireOp",EDGE,"E68")}),1.0]])]});
            var Q1;
            Q1=sQuery(id+"F43.wireOp",EDGE,"E68");
            extrude(context, id + "F57", {"entities" : qUnion([Q0]), "operationType" : NewBodyOperationType.REMOVE, "surfaceEntities" : qUnion([Q1]), "depth" : 9.43 * mm});
        }
        {
            var Q0;
            Q0=qCreatedBy(makeId("Top.planeOp"),FACE);
            var sketch = newSketch(context, id + "F58", { "sketchPlane" : qUnion([Q0])});
            skLineSegment(sketch, "E74.bottom", {"start": v(-64.67, -45.6) * mm, "end": v(-25.27, -45.6) * mm});
            skLineSegment(sketch, "E74.top", {"start": v(-64.67, -67.06) * mm, "end": v(-25.27, -67.06) * mm});
            skLineSegment(sketch, "E74.left", {"start": v(-64.67, -45.6) * mm, "end": v(-64.67, -67.06) * mm});
            skLineSegment(sketch, "E74.right", {"start": v(-25.27, -45.6) * mm, "end": v(-25.27, -67.06) * mm});
            skSolve(sketch);
        }
        {
            var Q0;
            Q0=makeQuery(id+"F58.imprint","IMPRINT",FACE,{"disambiguationData":[TD([[makeQuery(id+"F58.imprint","IMPRINT",EDGE,{"derivedFrom":sQuery(id+"F58.wireOp",EDGE,"E74.bottom")}),-1.0]])]});
            extrude(context, id + "F59", {"entities" : qUnion([Q0]), "operationType" : NewBodyOperationType.REMOVE, "oppositeDirection" : true, "depth" : 28.05 * mm});
        }
        {
            var Q0;
            Q0=makeQuery(id+"F58.imprint","IMPRINT",FACE,{"disambiguationData":[TD([[makeQuery(id+"F58.imprint","IMPRINT",EDGE,{"derivedFrom":sQuery(id+"F58.wireOp",EDGE,"E74.bottom")}),-1.0]])]});
            extrude(context, id + "F60", {"entities" : qUnion([Q0]), "operationType" : NewBodyOperationType.REMOVE, "depth" : 16.3 * mm});
        }
        {
            var Q0;
            {var subQ0=sQuery(id+"F58.wireOp",EDGE,"E74.bottom");Q0=makeQuery(id+"F60.boolean.opBoolean","MERGE",FACE,{"derivedFrom":[makeQuery(id+"F59.boolean.opBoolean","COPY",FACE,{"disambiguationData":[OD(1.0)],"derivedFrom":makeQuery(id+"F59.opExtrude","SWEPT_FACE",FACE,{"disambiguationData":[OSD([subQ0])]})}),makeQuery(id+"F60.opExtrude","SWEPT_FACE",FACE,{"disambiguationData":[OSD([subQ0])]})]});}
            var sketch = newSketch(context, id + "F61", { "sketchPlane" : qUnion([Q0])});
            skCircle(sketch, "E75", {"center": v(-53.34, 0) * mm, "radius": 7.62 * mm});
            skCircle(sketch, "E76", {"center": v(-40.17, -15.7) * mm, "radius": 7.62 * mm});
            skSolve(sketch);
        }
        {
            var Q0;
            Q0=makeQuery(id+"F61.imprint","IMPRINT",FACE,{"disambiguationData":[TD([[makeQuery(id+"F61.imprint","IMPRINT",EDGE,{"derivedFrom":sQuery(id+"F61.wireOp",EDGE,"E75")}),1.0]])]});
            extrude(context, id + "F62", {"entities" : qUnion([Q0]), "operationType" : NewBodyOperationType.REMOVE, "oppositeDirection" : true, "depth" : 12.7 * mm});
        }
        {
            var Q0;
            Q0=makeQuery(id+"F61.imprint","IMPRINT",FACE,{"disambiguationData":[TD([[makeQuery(id+"F61.imprint","IMPRINT",EDGE,{"derivedFrom":sQuery(id+"F61.wireOp",EDGE,"E76")}),1.0]])]});
            extrude(context, id + "F63", {"entities" : qUnion([Q0]), "operationType" : NewBodyOperationType.REMOVE, "oppositeDirection" : true, "depth" : 12.7 * mm});
        }
        {
            var Q0;
            {var subQ0=sQuery(id+"F3.wireOp",EDGE,"E32");var subQ1=sQuery(id+"F3.wireOp",EDGE,"E27");var subQ2=makeQuery(id+"F3.imprint","INTERSECT",VERTEX,{"disambiguationData":[OD(0.0)],"derivedFrom":[subQ1,subQ0]});Q0=makeQuery(id+"F3.imprint","IMPRINT",FACE,{"disambiguationData":[TD([[makeQuery(id+"F3.imprint","IMPRINT",EDGE,{"disambiguationData":[TD([[subQ2,-1.0]])],"derivedFrom":subQ1}),1.0]])]});}
            var Q1;
            {var subQ1=sQuery(id+"F3.wireOp",EDGE,"E29");Q1=makeQuery(id+"F3.imprint","IMPRINT",FACE,{"disambiguationData":[TD([[makeQuery(id+"F3.imprint","IMPRINT",EDGE,{"derivedFrom":subQ1}),-1.0]])]});}
            var Q2;
            {var subQ0=sQuery(id+"F3.wireOp",EDGE,"E30");var subQ1=sQuery(id+"F3.wireOp",EDGE,"E27");var subQ2=makeQuery(id+"F3.imprint","INTERSECT",VERTEX,{"derivedFrom":[subQ1,subQ0]});Q2=makeQuery(id+"F3.imprint","IMPRINT",FACE,{"disambiguationData":[TD([[makeQuery(id+"F3.imprint","IMPRINT",EDGE,{"disambiguationData":[TD([[subQ2,1.0]])],"derivedFrom":subQ1}),1.0]])]});}
            var Q3;
            {var subQ0=sQuery(id+"F3.wireOp",EDGE,"E30");var subQ1=sQuery(id+"F3.wireOp",EDGE,"E27");var subQ2=makeQuery(id+"F3.imprint","INTERSECT",VERTEX,{"derivedFrom":[subQ1,subQ0]});Q3=makeQuery(id+"F3.imprint","IMPRINT",FACE,{"disambiguationData":[TD([[makeQuery(id+"F3.imprint","IMPRINT",EDGE,{"disambiguationData":[TD([[subQ2,-1.0]])],"derivedFrom":subQ1}),1.0]])]});}
            var Q4;
            {var subQ1=sQuery(id+"F3.wireOp",EDGE,"E29");Q4=makeQuery(id+"F3.imprint","IMPRINT",FACE,{"disambiguationData":[TD([[makeQuery(id+"F3.imprint","IMPRINT",EDGE,{"derivedFrom":subQ1}),1.0]])]});}
            var Q5;
            Q5=sQuery(id+"F1.wireOp",EDGE,"E22");
            var Q6;
            Q6=sQuery(id+"F1.wireOp",EDGE,"E23");
            var Q7;
            Q7=sQuery(id+"F1.wireOp",EDGE,"E26");
            var Q8;
            Q8 = qConstructionFilter(qBodyType(qCreatedBy(id + "F66" ,EDGE), BodyType.WIRE), ConstructionObject.NO);
            sweep(context, id + "F64", {"operationType" : NewBodyOperationType.ADD, "profiles" : qUnion([Q0, Q1, Q2, Q3, Q4]), "path" : qUnion([Q5, Q6, Q7, Q8])});
        }
        {
            var Q0;
            Q0=sQuery(id+"F1.wireOp",EDGE,"E26");
            cPlane(context, id + "F65", {"entities" : qUnion([Q0]), "cplaneType" : CPlaneType.LINE_ANGLE, "offset" : 25.4 * mm, "angle" : 0 * degree, "width" : 152.4 * mm, "height" : 152.4 * mm});
        }
        {
            var Q0;
            Q0=qCreatedBy(id+"F65.planeOp",FACE);
            var sketch = newSketch(context, id + "F66", { "sketchPlane" : qUnion([Q0])});
            skLineSegment(sketch, "E77", {"start": v(-72.9, 0) * mm, "end": v(-74.78, 0) * mm});
            skArc(sketch, "E78", {"start": v(-74.78, 0) * mm, "mid": v(-85.02, 4.24) * mm, "end": v(-89.27, 14.48) * mm});
            skLineSegment(sketch, "E79", {"start": v(-89.27, 14.48) * mm, "end": v(-89.27, 29.42) * mm});
            skSolve(sketch);
        }
        {
            var Q0;
            Q0=makeQuery(id+"F64.opSweep","CAP_FACE",FACE,{"disambiguationData":[OSD([sQuery(id+"F1.wireOp",VERTEX,"E26.end"),sQuery(id+"F3.wireOp",EDGE,"E27"),sQuery(id+"F3.wireOp",EDGE,"E28")])],"isStart":false});
            var Q1;
            Q1=sQuery(id+"F66.wireOp",EDGE,"E77");
            var Q2;
            Q2=sQuery(id+"F66.wireOp",EDGE,"E78");
            var Q3;
            Q3=sQuery(id+"F66.wireOp",EDGE,"E79");
            sweep(context, id + "F67", {"operationType" : NewBodyOperationType.ADD, "profiles" : qUnion([Q0]), "path" : qUnion([Q1, Q2, Q3])});
        }
        {
            var Q0;
            Q0=makeQuery(id+"F18.opSweep","CAP_FACE",FACE,{"disambiguationData":[OSD([sQuery(id+"F3.wireOp",EDGE,"E31"),sQuery(id+"F3.wireOp",EDGE,"E32"),sQuery(id+"F5.wireOp",VERTEX,"E35.end")])],"isStart":false});
            extrude(context, id + "F68", {"entities" : qUnion([Q0]), "operationType" : NewBodyOperationType.ADD, "depth" : 12.7 * mm});
        }
        {
            var Q0;
            Q0=makeQuery(id+"F67.opSweep","CAP_FACE",FACE,{"disambiguationData":[OSD([sQuery(id+"F1.wireOp",VERTEX,"E26.end"),sQuery(id+"F3.wireOp",EDGE,"E27"),sQuery(id+"F3.wireOp",EDGE,"E28"),sQuery(id+"F66.wireOp",VERTEX,"E79.end")])],"isStart":false});
            var sketch = newSketch(context, id + "F69", { "sketchPlane" : qUnion([Q0])});
            skCircle(sketch, "E80", {"center": v(-89.27, 4.34) * mm, "radius": 7.62 * mm});
            skSolve(sketch);
        }
        {
            var Q0;
            Q0=makeQuery(id+"F68.opExtrude","CAP_FACE",FACE,{"disambiguationData":[OSD([sQuery(id+"F3.wireOp",EDGE,"E31"),sQuery(id+"F3.wireOp",EDGE,"E32"),sQuery(id+"F5.wireOp",VERTEX,"E35.end")])],"isStart":false});
            var sketch = newSketch(context, id + "F70", { "sketchPlane" : qUnion([Q0])});
            skCircle(sketch, "E81", {"center": v(-40.26, -33.05) * mm, "radius": 7.62 * mm});
            skSolve(sketch);
        }
        {
            var Q0;
            Q0=makeQuery(id+"F69.imprint","IMPRINT",FACE,{"disambiguationData":[TD([[makeQuery(id+"F69.imprint","IMPRINT",EDGE,{"derivedFrom":sQuery(id+"F69.wireOp",EDGE,"E80")}),1.0]])]});
            extrude(context, id + "F71", {"entities" : qUnion([Q0]), "operationType" : NewBodyOperationType.REMOVE, "oppositeDirection" : true, "depth" : 12.7 * mm});
        }
        {
            var Q0;
            Q0=makeQuery(id+"F70.imprint","IMPRINT",FACE,{"disambiguationData":[TD([[makeQuery(id+"F70.imprint","IMPRINT",EDGE,{"derivedFrom":sQuery(id+"F70.wireOp",EDGE,"E81")}),1.0]])]});
            extrude(context, id + "F72", {"entities" : qUnion([Q0]), "operationType" : NewBodyOperationType.REMOVE, "oppositeDirection" : true, "depth" : 12.7 * mm});
        }
        {
            var Q0;
            Q0=makeQuery(id+"F45.opSweep","CAP_FACE",FACE,{"disambiguationData":[OSD([sQuery(id+"F43.wireOp",EDGE,"E70"),sQuery(id+"F43.wireOp",EDGE,"E71"),sQuery(id+"F44.wireOp",VERTEX,"E72.end")])],"isStart":false});
            var sketch = newSketch(context, id + "F73", { "sketchPlane" : qUnion([Q0])});
            skCircle(sketch, "E82", {"center": v(0, 0) * mm, "radius": 7.62 * mm});
            skSolve(sketch);
        }
        {
            var Q0;
            Q0 = qSketchRegion(id + "F73", true);
            extrude(context, id + "F74", {"entities" : qUnion([Q0]), "operationType" : NewBodyOperationType.REMOVE, "oppositeDirection" : true, "depth" : 12.7 * mm});
        }
        {
            var Q0;
            Q0=makeQuery(id+"F46.opSweep","CAP_FACE",FACE,{"disambiguationData":[OSD([sQuery(id+"F43.wireOp",EDGE,"E68"),sQuery(id+"F43.wireOp",EDGE,"E69"),sQuery(id+"F44.wireOp",VERTEX,"E73.end")])],"isStart":false});
            var sketch = newSketch(context, id + "F75", { "sketchPlane" : qUnion([Q0])});
            skCircle(sketch, "E83", {"center": v(40.17, 0) * mm, "radius": 7.62 * mm});
            skSolve(sketch);
        }
        {
            var Q0;
            Q0=makeQuery(id+"F75.imprint","IMPRINT",FACE,{"disambiguationData":[TD([[makeQuery(id+"F75.imprint","IMPRINT",EDGE,{"derivedFrom":sQuery(id+"F75.wireOp",EDGE,"E83")}),1.0]])]});
            extrude(context, id + "F76", {"entities" : qUnion([Q0]), "operationType" : NewBodyOperationType.REMOVE, "oppositeDirection" : true, "depth" : 12.7 * mm});
        }
        {
            var Q0;
            Q0=makeQuery(id+"F68.opExtrude","CAP_FACE",FACE,{"disambiguationData":[OSD([sQuery(id+"F3.wireOp",EDGE,"E31"),sQuery(id+"F3.wireOp",EDGE,"E32"),sQuery(id+"F5.wireOp",VERTEX,"E35.end")])],"isStart":false});
            var sketch = newSketch(context, id + "F77", { "sketchPlane" : qUnion([Q0])});
            skCircle(sketch, "E84", {"center": v(-40.26, -33.05) * mm, "radius": 7.62 * mm});
            skSolve(sketch);
        }
        {
            var Q0;
            Q0=makeQuery(id+"F77.imprint","IMPRINT",FACE,{"disambiguationData":[TD([[makeQuery(id+"F77.imprint","IMPRINT",EDGE,{"derivedFrom":sQuery(id+"F77.wireOp",EDGE,"E84")}),1.0]])]});
            extrude(context, id + "F78", {"entities" : qUnion([Q0]), "operationType" : NewBodyOperationType.REMOVE, "oppositeDirection" : true, "depth" : 12.7 * mm});
        }
    });
